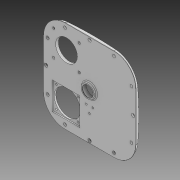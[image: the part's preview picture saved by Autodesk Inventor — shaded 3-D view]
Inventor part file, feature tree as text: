
AUTODESK INVENTOR PART (.ipt)
format: ipt  version: 2020 (Build 240168000, 168)  size: 919,552 bytes
history: native  units: mm
features: sketch x24, extrude x21, projected_geometry x6, other x4, plane x3, revolve x2, loft x1, fillet x1, chamfer x1
ambient origin geometry x8: Origin, YZ Plane, XZ Plane, XY Plane, X Axis, Y Axis, Z Axis, Center Point
bodies: Solid1 (feature_tree)
feature tree (63):
  other  "Blocks"
  sketch  "Sketch1"  dims[d1=170.0mm d2=170.0mm]
  extrude  "Extrusion1"  Depth=170.0mm
  extrude  "Extrusion2"  Depth=60.0mm TaperAngle=0.0deg
  plane  "Work Plane1"
  loft  "Loft1"
  extrude  "Extrusion3"  Depth=7.5mm
  plane  "Work Plane2"
  sketch  "Sketch6"  dims[d14=17.5mm d15=7.5mm]
  plane  "Work Plane3"
  sketch  "Sketch7"  dims[d16=10.0mm d17=65.0mm]
  extrude  "Extrusion4"  Depth=7.5mm
  extrude  "Extrusion5"  Depth=7.5mm
  extrude  "Extrusion9"  Depth=65.0mm
  sketch  "Sketch13"  dims[d23=0.0mm d24=90.0deg d25=5.0mm d26=0.0mm]
  extrude  "Extrusion10"  Depth=7.5mm
  extrude  "Extrusion11"  TaperAngle=0.0deg  [1 undecoded]
  extrude  "Extrusion12"  Depth=5.0mm TaperAngle=0.0deg
  revolve  "Revolution1"  [1 undecoded]
  extrude  "Extrusion13"  Depth=4.0mm
  extrude  "Extrusion14"  Depth=145.0mm
  extrude  "Extrusion15"  Depth=60.0mm TaperAngle=0.0deg
  revolve  "Revolution2"  [1 undecoded]
  fillet  "Fillet1"  Radius=47.0mm
  extrude  "Extrusion19"  Depth=60.0mm
  extrude  "Extrusion20"  Depth=42.426407mm
  extrude  "Extrusion22"  Depth=40.0mm
  extrude  "Extrusion23"  Depth=22.1mm
  extrude  "Extrusion24"  Depth=6.0mm TaperAngle=0.0deg
  extrude  "Extrusion25"  Depth=47.7mm
  extrude  "Extrusion17"  Depth=3.0mm
  extrude  "Extrusion18"  Depth=8.2mm
  extrude  "Extrusion26"  Depth=1.0mm
  chamfer  "Chamfer1"  Angle=90.0deg  [1 undecoded]
  sketch  "Sketch2"  dims[d3=40.0mm d4=60.0mm d5=0.0mm]
  other  "Block1"
  sketch  "Sketch3"  dims[d7=0.0mm d8=0.0mm d9=5.5mm]
  sketch  "Sketch4"  dims[d10=57.5mm d11=7.5mm]
  projected_geometry  "Projected Loop1"
  sketch  "Sketch5"  dims[d12=7.5mm d13=7.5mm]
  projected_geometry  "Projected Loop2"
  projected_geometry  "Projected Loop3"
  projected_geometry  "Projected Loop4"
  sketch  "Sketch8"  dims[d18=7.5mm d19=7.5mm]
  sketch  "Sketch12"  dims[d20=25.0mm d21=0.0mm d22=90.0deg]
  projected_geometry  "Projected Loop5"
  sketch  "Sketch14"  dims[d27=180.0mm d28=-3.0mm]
  sketch  "Sketch15"  dims[d29=2.5mm d30=4.0mm]
  sketch  "Sketch16"  dims[d31=10.0mm d32=0.0mm d33=145.0mm]
  sketch  "Sketch17"  dims[d34=48.25mm d35=0.0mm d54=60.0mm d55=0.0mm]
  sketch  "Sketch18"  dims[d56=5.0mm d57=0.0mm d58=47.0mm d59=47.0mm]
  sketch  "Sketch21"  dims[d60=60.0mm d61=60.0mm]
  sketch  "Sketch22"  dims[d62=42.426407mm d63=42.426407mm]
  sketch  "Sketch23"  dims[d64=4.4mm d65=40.0mm]
  sketch  "Sketch24"  dims[d66=6.0mm d67=0.0mm d68=22.1mm]
  sketch  "Sketch26"  dims[d69=16.0mm d70=6.0mm d71=0.0mm]
  sketch  "Sketch27"  dims[d72=35.0mm d73=47.7mm]
  sketch  "Sketch28"  dims[d74=25.0mm d75=3.0mm]
  sketch  "Sketch29"  dims[d77=7.2mm d78=8.2mm]
  sketch  "Sketch30"  dims[d79=0.5mm d80=1.0mm d81=90.0deg d82=60.0mm d83=10.0mm d85=5.5mm d86=9.0mm d87=40.0mm d89=360.0deg d91=48.25mm d92=0.0mm d93=9.5mm d94=40.0mm d96=360.0deg d98=16.0mm d99=0.0mm d100=0.0mm d101=0.0mm d106=12.0mm d107=12.0mm d109=3.3mm d110=0.0mm d111=0.0mm d112=7.0mm d113=135.0deg d114=0.5mm d115=1.0mm d116=2.0mm d117=19.198622mm d118=90.0deg d119=2.0mm d120=5.8mm d121=2.5mm d122=0.0mm d124=10.0mm d125=0.0mm d126=50.0mm d127=50.0mm d128=40.0mm d129=48.0mm d130=3.3mm d133=0.0mm d134=0.0mm d139=43.0mm d140=43.0mm d141=50.5mm d142=2.0mm d143=0.0mm d144=80.0mm d145=3.5mm d146=40.0mm d148=360.0deg d150=0.0mm d151=0.0mm d152=6.0mm d153=3.0mm d154=0.0mm d155=7.3mm d156=2.0mm d157=0.0mm d158=25.0mm d159=90.0deg d160=1.5mm d161=0.0mm d162=32.0mm d163=0.5mm d164=2.0mm d165=45.0deg]
  projected_geometry  "Projected Loop6"
  other  "Block1:1"
  other  "Block1:2"
note: 4 required parameter values undecoded (feature->parameter linkage not recoverable at this tier; creation-order binding heuristic only, values carry confidence <= 0.55)